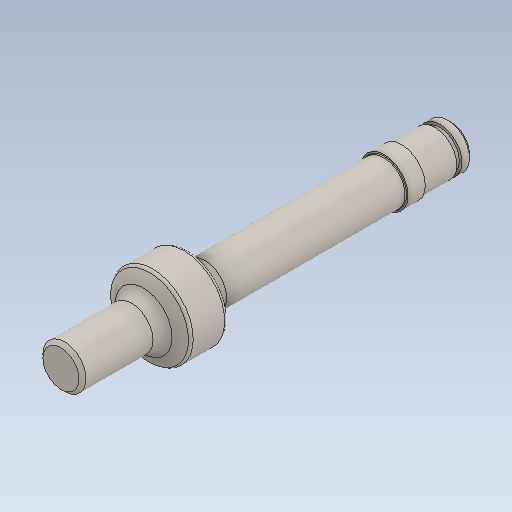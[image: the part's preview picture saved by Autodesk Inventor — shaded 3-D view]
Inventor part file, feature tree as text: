
AUTODESK INVENTOR PART (.ipt)
format: ipt  version: 2020 (Build 240168000, 168)  size: 156,160 bytes
history: native  units: in
note: dims shown in document units (in); Inventor stores cm internally (conversion verified against a paired STEP export)
features: fillet x1
ambient origin geometry x8: Origin, YZ Plane, XZ Plane, XY Plane, X Axis, Y Axis, Z Axis, Center Point
bodies: Solid1 (feature_tree)
feature tree (1):
  fillet  "Fillet2"  [1 undecoded]
note: 1 required parameter value undecoded (feature->parameter linkage not recoverable at this tier; creation-order binding heuristic only, values carry confidence <= 0.55)
